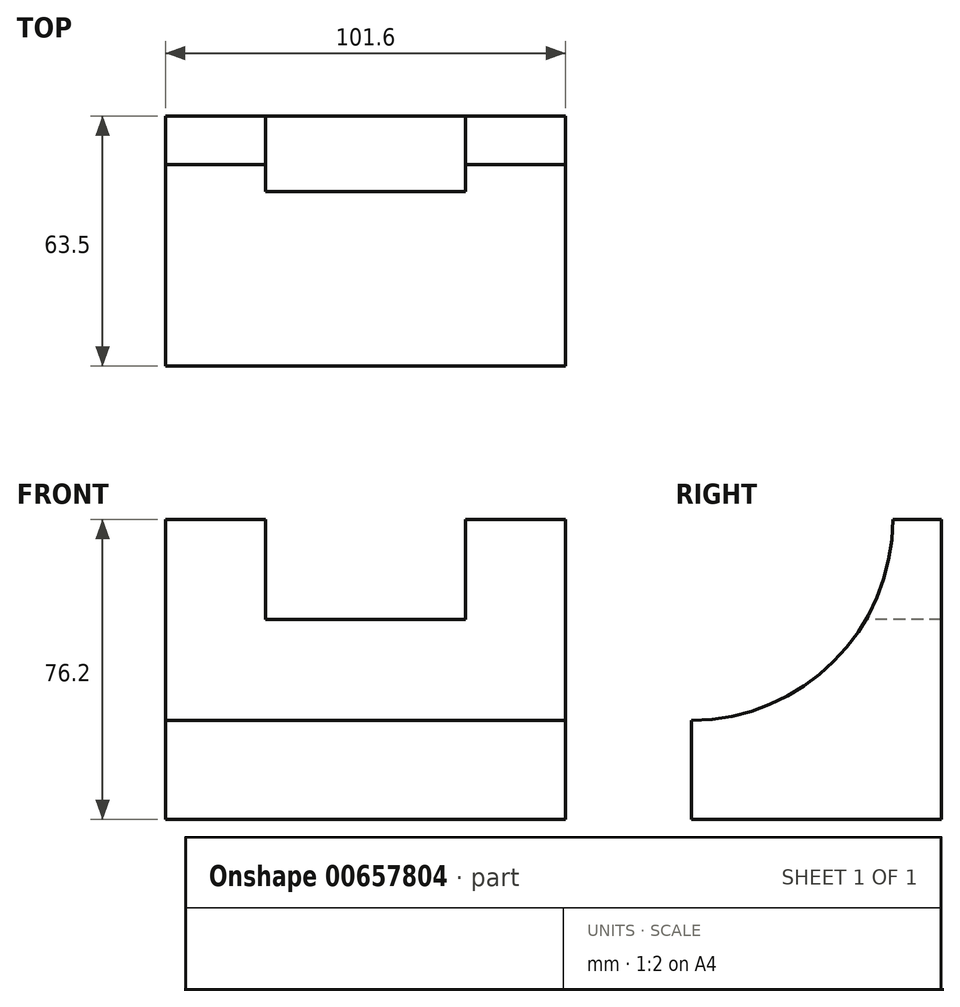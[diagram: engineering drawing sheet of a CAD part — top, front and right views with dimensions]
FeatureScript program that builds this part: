
annotation { "Feature Type Name" : "Feature", "Feature Type Description" : "" }
export const myFeature = defineFeature(function(context is Context, id is Id, definition is map)
    precondition{}
    {
        {
            var Q0;
            Q0=qCreatedBy(makeId("Top.planeOp"),FACE);
            var sketch = newSketch(context, id + "F0", { "sketchPlane" : qUnion([Q0])});
            skLineSegment(sketch, "E0.bottom", {"start": v(-3.3, 10.2) * mm, "end": v(98.3, 10.2) * mm});
            skLineSegment(sketch, "E0.top", {"start": v(-3.3, -53.3) * mm, "end": v(98.3, -53.3) * mm});
            skLineSegment(sketch, "E0.left", {"start": v(-3.3, 10.2) * mm, "end": v(-3.3, -53.3) * mm});
            skLineSegment(sketch, "E0.right", {"start": v(98.3, 10.2) * mm, "end": v(98.3, -53.3) * mm});
            skSolve(sketch);
        }
        {
            var Q0;
            Q0 = qSketchRegion(id + "F0", true);
            extrude(context, id + "F1", {"entities" : qUnion([Q0]), "depth" : 25.4 * mm, "offsetDistance" : 25.4 * mm});
        }
        {
            var Q0;
            Q0=makeQuery(id+"F1.opExtrude","CAP_FACE",FACE,{"disambiguationData":[OSD([sQuery(id+"F0.wireOp",EDGE,"E0.bottom"),sQuery(id+"F0.wireOp",EDGE,"E0.top"),sQuery(id+"F0.wireOp",EDGE,"E0.left"),sQuery(id+"F0.wireOp",EDGE,"E0.right")])],"isStart":false});
            extrude(context, id + "F2", {"entities" : qUnion([Q0]), "operationType" : NewBodyOperationType.ADD, "depth" : 50.8 * mm, "offsetDistance" : 25.4 * mm});
        }
        {
            var Q0;
            {var subQ0=sQuery(id+"F0.wireOp",EDGE,"E0.right");Q0=makeQuery(id+"F2.boolean.opBoolean","MERGE",FACE,{"derivedFrom":[makeQuery(id+"F1.opExtrude","SWEPT_FACE",FACE,{"disambiguationData":[OSD([subQ0])]}),makeQuery(id+"F2.opExtrude","SWEPT_FACE",FACE,{"disambiguationData":[OSD([subQ0])]})]});}
            var sketch = newSketch(context, id + "F3", { "sketchPlane" : qUnion([Q0])});
            skLineSegment(sketch, "E1", {"start": v(10.2, 76.2) * mm, "end": v(-2.5, 76.2) * mm});
            skLineSegment(sketch, "E2", {"start": v(-53.3, 0) * mm, "end": v(-53.3, 25.4) * mm});
            skSolve(sketch);
        }
        {
            var Q0;
            {var subQ5=sQuery(id+"F3.wireOp",EDGE,"E1");Q0=makeQuery(id+"F3.imprint","IMPRINT",FACE,{"disambiguationData":[TD([[makeQuery(id+"F3.imprint","IMPRINT",EDGE,{"derivedFrom":subQ5}),1.0]])]});}
            var sketch = newSketch(context, id + "F4", { "sketchPlane" : qUnion([Q0])});
            skCircle(sketch, "E3", {"center": v(-53.44, 76.44) * mm, "radius": 51.33 * mm});
            skSolve(sketch);
        }
        {
            var Q0;
            Q0 = qSketchRegion(id + "F4", true);
            extrude(context, id + "F5", {"entities" : qUnion([Q0]), "operationType" : NewBodyOperationType.REMOVE, "oppositeDirection" : true, "depth" : 117.6 * mm, "offsetDistance" : 25.4 * mm});
        }
        {
            var Q0;
            Q0=makeQuery(id+"F2.opExtrude","CAP_FACE",FACE,{"disambiguationData":[OSD([sQuery(id+"F0.wireOp",EDGE,"E0.bottom"),sQuery(id+"F0.wireOp",EDGE,"E0.top"),sQuery(id+"F0.wireOp",EDGE,"E0.left"),sQuery(id+"F0.wireOp",EDGE,"E0.right")])],"isStart":false});
            var sketch = newSketch(context, id + "F6", { "sketchPlane" : qUnion([Q0])});
            skLineSegment(sketch, "E4", {"start": v(-3.3, 10.2) * mm, "end": v(22.1, 10.2) * mm});
            skLineSegment(sketch, "E5", {"start": v(98.3, 10.2) * mm, "end": v(72.9, 10.2) * mm});
            skLineSegment(sketch, "E6.bottom", {"start": v(22.1, 10.2) * mm, "end": v(72.9, 10.2) * mm});
            skLineSegment(sketch, "E6.top", {"start": v(22.1, -2.11) * mm, "end": v(72.9, -2.11) * mm});
            skLineSegment(sketch, "E6.left", {"start": v(22.1, 10.2) * mm, "end": v(22.1, -2.11) * mm});
            skLineSegment(sketch, "E6.right", {"start": v(72.9, 10.2) * mm, "end": v(72.9, -2.11) * mm});
            skSolve(sketch);
        }
        {
            var Q0;
            Q0=makeQuery(id+"F6.imprint","IMPRINT",FACE,{"disambiguationData":[TD([[makeQuery(id+"F6.imprint","IMPRINT",EDGE,{"derivedFrom":sQuery(id+"F6.wireOp",EDGE,"E6.bottom")}),-1.0]])]});
            extrude(context, id + "F7", {"entities" : qUnion([Q0]), "operationType" : NewBodyOperationType.REMOVE, "oppositeDirection" : true, "depth" : 25.4 * mm, "offsetDistance" : 25.4 * mm});
        }
        {
            var Q0;
            Q0=makeQuery(id+"F7.boolean.opBoolean","COPY",FACE,{"derivedFrom":makeQuery(id+"F7.opExtrude","SWEPT_FACE",FACE,{"disambiguationData":[OSD([sQuery(id+"F6.wireOp",EDGE,"E6.top")])]})});
            extrude(context, id + "F8", {"entities" : qUnion([Q0]), "operationType" : NewBodyOperationType.REMOVE, "oppositeDirection" : true, "depth" : 25.4 * mm, "offsetDistance" : 25.4 * mm});
        }
    });
